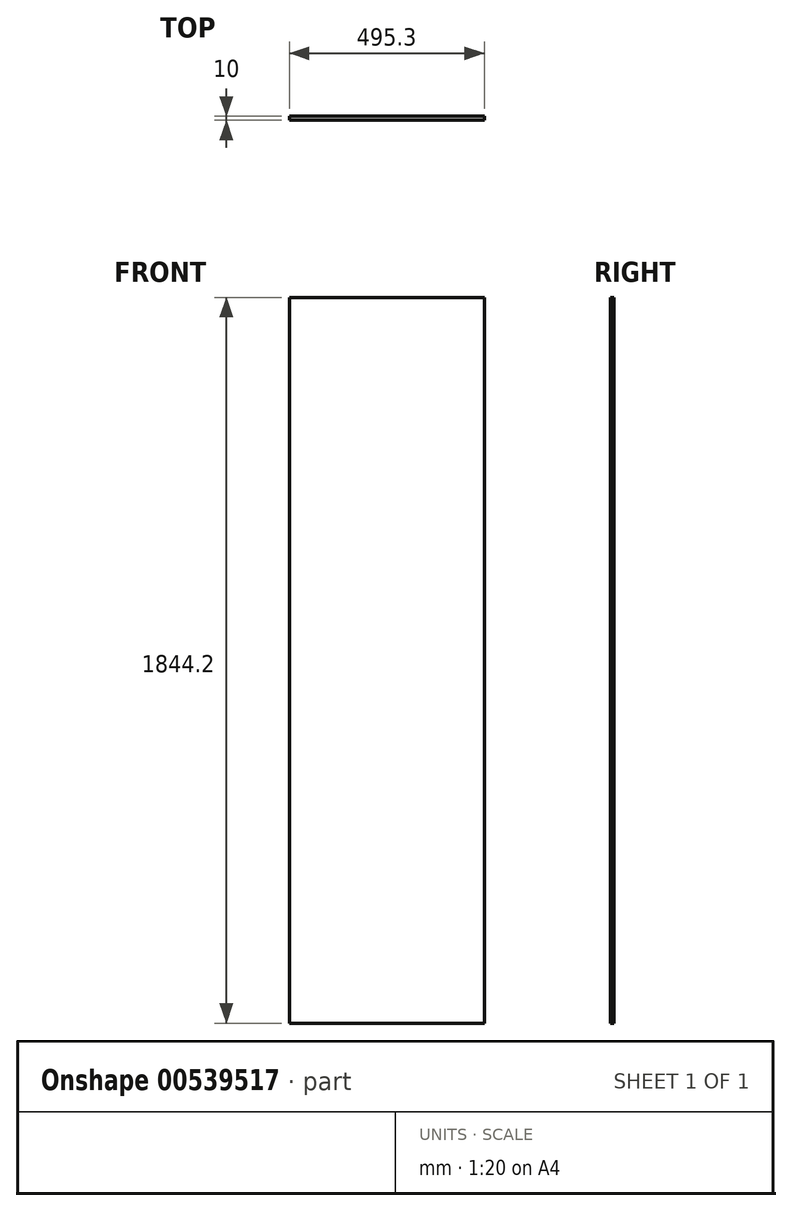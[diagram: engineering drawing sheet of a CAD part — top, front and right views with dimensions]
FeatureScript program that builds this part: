
annotation { "Feature Type Name" : "Feature", "Feature Type Description" : "" }
export const myFeature = defineFeature(function(context is Context, id is Id, definition is map)
    precondition{}
    {
        {
            var Q0;
            Q0=qCreatedBy(makeId("Front.planeOp"),FACE);
            var sketch = newSketch(context, id + "F0", { "sketchPlane" : qUnion([Q0])});
            skLineSegment(sketch, "E0.bottom", {"start": v(247.65, -922.1) * mm, "end": v(-247.65, -922.1) * mm});
            skLineSegment(sketch, "E0.top", {"start": v(247.65, 922.1) * mm, "end": v(-247.65, 922.1) * mm});
            skLineSegment(sketch, "E0.left", {"start": v(247.65, -922.1) * mm, "end": v(247.65, 922.1) * mm});
            skLineSegment(sketch, "E0.right", {"start": v(-247.65, -922.1) * mm, "end": v(-247.65, 922.1) * mm});
            skPoint(sketch, "E0.middle", {"position": v(0, 0) * mm});
            skSolve(sketch);
        }
        {
            var Q0;
            Q0=makeQuery(id+"F0.imprint","IMPRINT",FACE,{"disambiguationData":[TD([[makeQuery(id+"F0.imprint","IMPRINT",EDGE,{"derivedFrom":sQuery(id+"F0.wireOp",EDGE,"E0.bottom")}),-1.0]])]});
            extrude(context, id + "F1", {"entities" : qUnion([Q0]), "depth" : 10 * mm});
        }
    });
